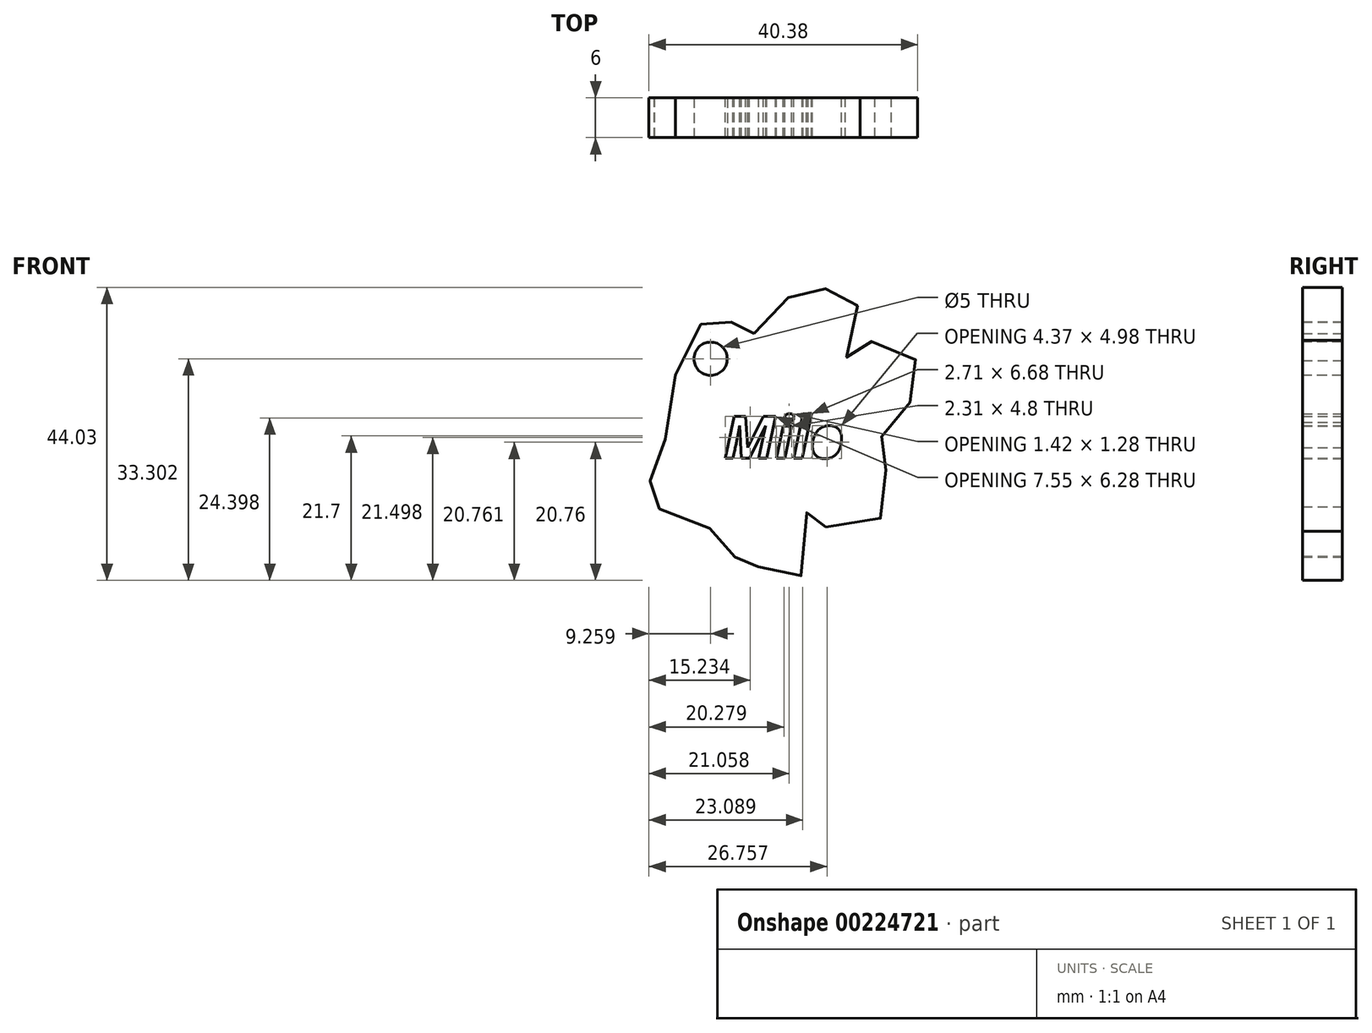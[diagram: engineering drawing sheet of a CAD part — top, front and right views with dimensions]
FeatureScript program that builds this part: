
annotation { "Feature Type Name" : "Feature", "Feature Type Description" : "" }
export const myFeature = defineFeature(function(context is Context, id is Id, definition is map)
    precondition{}
    {
        {
            var Q0;
            Q0=qCreatedBy(makeId("Front.planeOp"),FACE);
            var sketch = newSketch(context, id + "F0", { "sketchPlane" : qUnion([Q0])});
            skLineSegment(sketch, "E0.bottom", {"start": v(3.87, 7.52) * mm, "end": v(48.87, 7.52) * mm});
            skLineSegment(sketch, "E0.top", {"start": v(3.87, -37.48) * mm, "end": v(48.87, -37.48) * mm});
            skLineSegment(sketch, "E0.left", {"start": v(3.87, 7.52) * mm, "end": v(3.87, -37.48) * mm});
            skLineSegment(sketch, "E0.right", {"start": v(48.87, 7.52) * mm, "end": v(48.87, -37.48) * mm});
            skSolve(sketch);
        }
        {
            var Q0;
            Q0=makeQuery(id+"F0.imprint","IMPRINT",FACE,{"disambiguationData":[TD([[makeQuery(id+"F0.imprint","IMPRINT",EDGE,{"derivedFrom":sQuery(id+"F0.wireOp",EDGE,"E0.bottom")}),-1.0]])]});
            var sketch = newSketch(context, id + "F1", { "sketchPlane" : qUnion([Q0])});
            skFitSpline(sketch, "E1", {"points": [v(22.21, 0) * mm, v(19.9, 1.66) * mm, v(19.63, 1.75) * mm, v(16.68, 1.75) * mm, v(16.6, 1.75) * mm, v(11.8, 0) * mm, v(9.96, -14) * mm, v(6.55, -19.26) * mm, v(7.29, -25.71) * mm, v(7.29, -26.17) * mm, v(14.01, -27.83) * mm, v(18.16, -33.27) * mm, v(20, -33.55) * mm, v(20.55, -33.55) * mm, v(24.24, -35.94) * mm, v(29.5, -36.13) * mm, v(30.14, -26.08) * mm, v(31.52, -28.1) * mm, v(40.18, -28.66) * mm, v(42.58, -21.66) * mm, v(40.37, -17.42) * mm, v(43.68, -13.18) * mm, v(46.26, -8.76) * mm, v(46.08, -3.14) * mm, v(39.08, -1.48) * mm, v(35.96, -4.05) * mm, v(38.15, 3.04) * mm, v(34.75, 6.08) * mm, v(31.98, 6.9) * mm, v(27.19, 5.25) * mm, v(22.21, 0) * mm]});
            skText(sketch, "E2", { "text": "Milo ", "fontName": "OpenSans-BoldItalic.ttf"});
            const initialGuessF1  = {"E2": [0.01767, -0.01874, 1, 0, 0.00633]};
            skSetInitialGuess(sketch, initialGuessF1);
            skSolve(sketch);
        }
        {
            var Q0;
            Q0 = qSketchRegion(id + "F1", true);
            var Q1;
            Q1=sQuery(id+"F1.wireOp",EDGE,"E1");
            extrude(context, id + "F2", {"entities" : qUnion([Q0]), "surfaceEntities" : qUnion([Q1]), "depth" : 6 * mm});
        }
        {
            var Q0;
            Q0=makeQuery(id+"F2.opExtrude","CAP_FACE",FACE,{"disambiguationData":[OSD([sQuery(id+"F1.wireOp",EDGE,"E1"),sQuery(id+"F1.wireOp",EDGE,"E2.sketch_text.stroke-0"),sQuery(id+"F1.wireOp",EDGE,"E2.sketch_text.stroke-1"),sQuery(id+"F1.wireOp",EDGE,"E2.sketch_text.stroke-2"),sQuery(id+"F1.wireOp",EDGE,"E2.sketch_text.stroke-3"),sQuery(id+"F1.wireOp",EDGE,"E2.sketch_text.stroke-4"),sQuery(id+"F1.wireOp",EDGE,"E2.sketch_text.stroke-5"),sQuery(id+"F1.wireOp",EDGE,"E2.sketch_text.stroke-6"),sQuery(id+"F1.wireOp",EDGE,"E2.sketch_text.stroke-7"),sQuery(id+"F1.wireOp",EDGE,"E2.sketch_text.stroke-8"),sQuery(id+"F1.wireOp",EDGE,"E2.sketch_text.stroke-9"),sQuery(id+"F1.wireOp",EDGE,"E2.sketch_text.stroke-10"),sQuery(id+"F1.wireOp",EDGE,"E2.sketch_text.stroke-11"),sQuery(id+"F1.wireOp",EDGE,"E2.sketch_text.stroke-12"),sQuery(id+"F1.wireOp",EDGE,"E2.sketch_text.stroke-13"),sQuery(id+"F1.wireOp",EDGE,"E2.sketch_text.stroke-14"),sQuery(id+"F1.wireOp",EDGE,"E2.sketch_text.stroke-15"),sQuery(id+"F1.wireOp",EDGE,"E2.sketch_text.stroke-16"),sQuery(id+"F1.wireOp",EDGE,"E2.sketch_text.stroke-17"),sQuery(id+"F1.wireOp",EDGE,"E2.sketch_text.stroke-18"),sQuery(id+"F1.wireOp",EDGE,"E2.sketch_text.stroke-19"),sQuery(id+"F1.wireOp",EDGE,"E2.sketch_text.stroke-20"),sQuery(id+"F1.wireOp",EDGE,"E2.sketch_text.stroke-21"),sQuery(id+"F1.wireOp",EDGE,"E2.sketch_text.stroke-22"),sQuery(id+"F1.wireOp",EDGE,"E2.sketch_text.stroke-23"),sQuery(id+"F1.wireOp",EDGE,"E2.sketch_text.stroke-24"),sQuery(id+"F1.wireOp",EDGE,"E2.sketch_text.stroke-25"),sQuery(id+"F1.wireOp",EDGE,"E2.sketch_text.stroke-26"),sQuery(id+"F1.wireOp",EDGE,"E2.sketch_text.stroke-27"),sQuery(id+"F1.wireOp",EDGE,"E2.sketch_text.stroke-28"),sQuery(id+"F1.wireOp",EDGE,"E2.sketch_text.stroke-29"),sQuery(id+"F1.wireOp",EDGE,"E2.sketch_text.stroke-30"),sQuery(id+"F1.wireOp",EDGE,"E2.sketch_text.stroke-31"),sQuery(id+"F1.wireOp",EDGE,"E2.sketch_text.stroke-32"),sQuery(id+"F1.wireOp",EDGE,"E2.sketch_text.stroke-41"),sQuery(id+"F1.wireOp",EDGE,"E2.sketch_text.stroke-42"),sQuery(id+"F1.wireOp",EDGE,"E2.sketch_text.stroke-43"),sQuery(id+"F1.wireOp",EDGE,"E2.sketch_text.stroke-44"),sQuery(id+"F1.wireOp",EDGE,"E2.sketch_text.stroke-45"),sQuery(id+"F1.wireOp",EDGE,"E2.sketch_text.stroke-46"),sQuery(id+"F1.wireOp",EDGE,"E2.sketch_text.stroke-47"),sQuery(id+"F1.wireOp",EDGE,"E2.sketch_text.stroke-48"),sQuery(id+"F1.wireOp",EDGE,"E2.sketch_text.stroke-49"),sQuery(id+"F1.wireOp",EDGE,"E2.sketch_text.stroke-50")])],"isStart":false});
            var sketch = newSketch(context, id + "F3", { "sketchPlane" : qUnion([Q0])});
            skPoint(sketch, "E3", {"position": v(15.7, -3.8) * mm});
            skSolve(sketch);
        }
        {
            var Q0;
            Q0=sQuery(id+"F3.wireOp",VERTEX,"E3");
            var Q1;
            Q1=makeQuery(id+"F2.opExtrude","SWEPT_BODY",BODY,{"disambiguationData":[OSD([sQuery(id+"F1.wireOp",EDGE,"E1"),sQuery(id+"F1.wireOp",EDGE,"E2.sketch_text.stroke-0"),sQuery(id+"F1.wireOp",EDGE,"E2.sketch_text.stroke-1"),sQuery(id+"F1.wireOp",EDGE,"E2.sketch_text.stroke-2"),sQuery(id+"F1.wireOp",EDGE,"E2.sketch_text.stroke-3"),sQuery(id+"F1.wireOp",EDGE,"E2.sketch_text.stroke-4"),sQuery(id+"F1.wireOp",EDGE,"E2.sketch_text.stroke-5"),sQuery(id+"F1.wireOp",EDGE,"E2.sketch_text.stroke-6"),sQuery(id+"F1.wireOp",EDGE,"E2.sketch_text.stroke-7"),sQuery(id+"F1.wireOp",EDGE,"E2.sketch_text.stroke-8"),sQuery(id+"F1.wireOp",EDGE,"E2.sketch_text.stroke-9"),sQuery(id+"F1.wireOp",EDGE,"E2.sketch_text.stroke-10"),sQuery(id+"F1.wireOp",EDGE,"E2.sketch_text.stroke-11"),sQuery(id+"F1.wireOp",EDGE,"E2.sketch_text.stroke-12"),sQuery(id+"F1.wireOp",EDGE,"E2.sketch_text.stroke-13"),sQuery(id+"F1.wireOp",EDGE,"E2.sketch_text.stroke-14"),sQuery(id+"F1.wireOp",EDGE,"E2.sketch_text.stroke-15"),sQuery(id+"F1.wireOp",EDGE,"E2.sketch_text.stroke-16"),sQuery(id+"F1.wireOp",EDGE,"E2.sketch_text.stroke-17"),sQuery(id+"F1.wireOp",EDGE,"E2.sketch_text.stroke-18"),sQuery(id+"F1.wireOp",EDGE,"E2.sketch_text.stroke-19"),sQuery(id+"F1.wireOp",EDGE,"E2.sketch_text.stroke-20"),sQuery(id+"F1.wireOp",EDGE,"E2.sketch_text.stroke-21"),sQuery(id+"F1.wireOp",EDGE,"E2.sketch_text.stroke-22"),sQuery(id+"F1.wireOp",EDGE,"E2.sketch_text.stroke-23"),sQuery(id+"F1.wireOp",EDGE,"E2.sketch_text.stroke-24"),sQuery(id+"F1.wireOp",EDGE,"E2.sketch_text.stroke-25"),sQuery(id+"F1.wireOp",EDGE,"E2.sketch_text.stroke-26"),sQuery(id+"F1.wireOp",EDGE,"E2.sketch_text.stroke-27"),sQuery(id+"F1.wireOp",EDGE,"E2.sketch_text.stroke-28"),sQuery(id+"F1.wireOp",EDGE,"E2.sketch_text.stroke-29"),sQuery(id+"F1.wireOp",EDGE,"E2.sketch_text.stroke-30"),sQuery(id+"F1.wireOp",EDGE,"E2.sketch_text.stroke-31"),sQuery(id+"F1.wireOp",EDGE,"E2.sketch_text.stroke-32"),sQuery(id+"F1.wireOp",EDGE,"E2.sketch_text.stroke-41"),sQuery(id+"F1.wireOp",EDGE,"E2.sketch_text.stroke-42"),sQuery(id+"F1.wireOp",EDGE,"E2.sketch_text.stroke-43"),sQuery(id+"F1.wireOp",EDGE,"E2.sketch_text.stroke-44"),sQuery(id+"F1.wireOp",EDGE,"E2.sketch_text.stroke-45"),sQuery(id+"F1.wireOp",EDGE,"E2.sketch_text.stroke-46"),sQuery(id+"F1.wireOp",EDGE,"E2.sketch_text.stroke-47"),sQuery(id+"F1.wireOp",EDGE,"E2.sketch_text.stroke-48"),sQuery(id+"F1.wireOp",EDGE,"E2.sketch_text.stroke-49"),sQuery(id+"F1.wireOp",EDGE,"E2.sketch_text.stroke-50")])]});
            hole(context, id + "F4", {"style" : HoleStyle.SIMPLE, "endStyle" : HoleEndStyle.THROUGH, "holeDiameter" : 5 * mm, "locations" : qUnion([Q0]), "scope" : qUnion([Q1]), "isTappedThrough" : true});
        }
    });
